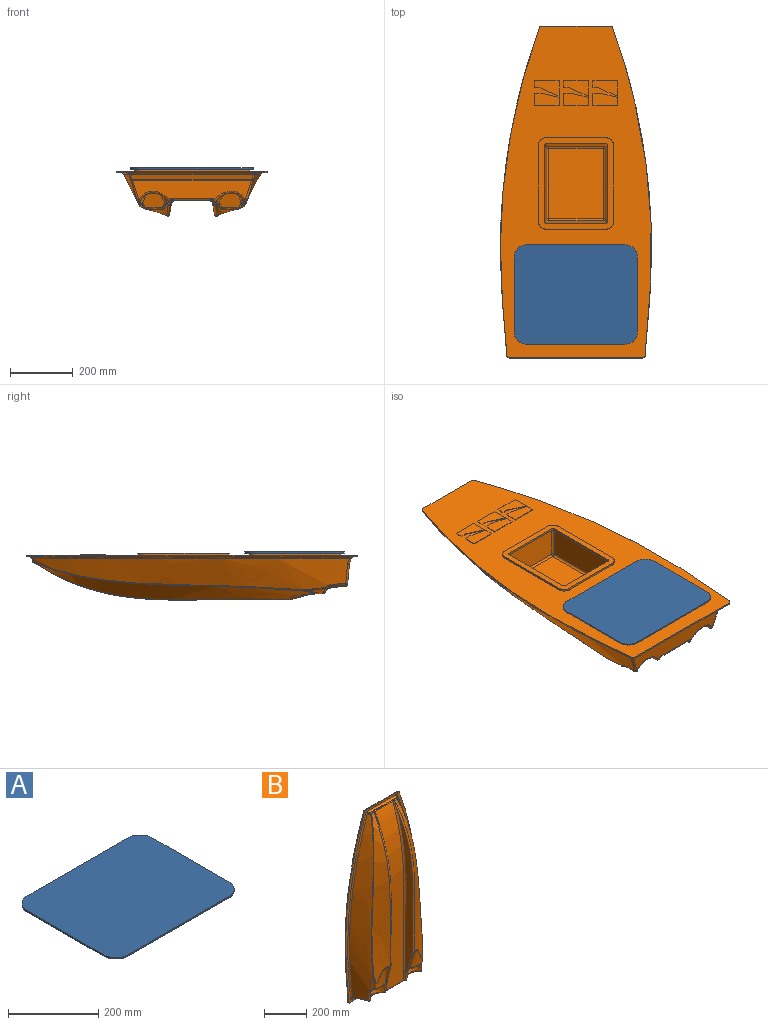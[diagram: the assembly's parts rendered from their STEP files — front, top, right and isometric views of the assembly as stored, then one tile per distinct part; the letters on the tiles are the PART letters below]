
ASSEMBLY  parts=2 mates=1
PART A: 10 faces, bbox 394x318x4 mm
  f0: plane 238x4mm, normal (-1,0,0), area 952mm2, adj f4,f5,f6,f9
  f1: plane 314x4mm, normal (0,-1,0), area 1256mm2, adj f4,f5,f6,f7
  f2: plane 238x4mm, normal (1,0,0), area 952mm2, adj f4,f5,f7,f8
  f3: plane 314x4mm, normal (0,1,0), area 1256mm2, adj f4,f5,f8,f9
  f4: plane 394x318mm, normal (0,0,1), area 123918.5mm2, adj f0,f1,f2,f3,f6,f7,f8,f9
  f5: plane 394x318mm, normal (0,0,-1), area 123918.5mm2, adj f0,f1,f2,f3,f6,f7,f8,f9
  f6: cylinder r=40mm len=40mm, axis (0,0,1), area 251.3mm2, adj f0,f1,f4,f5
  f7: cylinder r=40mm len=40mm, axis (0,0,-1), area 251.3mm2, adj f1,f2,f4,f5
  f8: cylinder r=40mm len=40mm, axis (0,0,1), area 251.3mm2, adj f2,f3,f4,f5
  f9: cylinder r=40mm len=40mm, axis (0,0,-1), area 251.3mm2, adj f0,f3,f4,f5
PART B: 255 faces, bbox 484.7x161.7x1062.5 mm
  f0: plane 1062.25x484.43mm, normal (0,1,0), area 254372.4mm2, adj f195,f196,f197,f198,f199,f200,f201,f202
  f1: sphere r=6.35mm, area 34mm2, adj f22,f26,f27
  f2: sphere r=6.35mm, area 34mm2, adj f32,f35,f36
  f3: sphere r=6.35mm, area 72.6mm2, adj f7,f8,f11,f40,f41
  f4: sphere r=6.35mm, area 72.6mm2, adj f10,f13,f14,f39,f42
  f5: sphere r=6.35mm, area 9.7mm2, adj f32,f43,f44
  f6: bspline ~1.26x0.54mm, area 0.2mm2, adj f31,f44,f45
  f7: bspline ~7.91x4.2mm, area 3.2mm2, adj f3,f11,f49,f87
  f8: bspline ~53.18x21.63mm, area 709.5mm2, adj f3,f22,f49,f69
  f9: bspline ~7.58x7.17mm, area 16mm2, adj f10,f39,f50
  f10: bspline ~9.73x6.62mm, area 49.8mm2, adj f4,f9,f14,f50
  f11: bspline ~9.73x6.62mm, area 49.8mm2, adj f3,f7,f12,f50
  f12: bspline ~7.58x7.17mm, area 16mm2, adj f11,f40,f50
  f13: bspline ~53.18x21.63mm, area 709.5mm2, adj f4,f35,f51,f80
  f14: bspline ~7.91x4.2mm, area 3.2mm2, adj f4,f10,f51,f87
  f15: bspline ~1016x132.22mm, area 25613.1mm2, adj f32,f35,f43,f53
  f16: sphere r=6.37mm, area 0.3mm2, adj f25,f56,f57
  f17: bspline ~1016x132.22mm, area 25875.6mm2, adj f22,f26,f47,f58
  f18: sphere r=6.35mm, area 9.7mm2, adj f26,f57,f58
  f19: bspline ~4.38x4.27mm, area 5.3mm2, adj f60,f62,f63
  f20: bspline ~4.38x4.27mm, area 5.3mm2, adj f61,f62,f65
  f21: plane 71.82x52.53mm, normal (0,-0.28,-0.96), area 2930.9mm2, adj f24,f28,f70
  f22: bspline ~16.78x12.12mm, area 106.9mm2, adj f1,f8,f17,f48,f70
  f23: bspline ~6.08x5.67mm, area 16.2mm2, adj f24,f28,f71
  f24: bspline ~14.85x9.65mm, area 114.2mm2, adj f21,f23,f29,f71
  f25: bspline ~1.31x0.96mm, area 0.2mm2, adj f16,f56,f71
  f26: bspline ~116.49x39.24mm, area 1463.5mm2, adj f1,f17,f18,f71
  f27: bspline ~9.52x6.58mm, area 40.3mm2, adj f1,f28,f70,f71
  f28: bspline ~70.09x19.29mm, area 611.2mm2, adj f21,f23,f27,f71
  f29: bspline ~6.82x6.46mm, area 30.8mm2, adj f24,f70,f71,f72
  f30: bspline ~14.85x9.65mm, area 114.2mm2, adj f34,f37,f38,f77
  f31: bspline ~1.31x0.96mm, area 0.2mm2, adj f6,f45,f77
  f32: bspline ~116.49x39.24mm, area 1463.5mm2, adj f2,f5,f15,f77
  f33: bspline ~70.09x19.29mm, area 611.5mm2, adj f34,f36,f37,f77
  f34: bspline ~6.08x5.68mm, area 16.4mm2, adj f30,f33,f77
  f35: bspline ~16.78x12.12mm, area 106.9mm2, adj f2,f13,f15,f52,f79
  f36: bspline ~9.52x6.58mm, area 40.3mm2, adj f2,f33,f77,f79
  f37: plane 71.84x52.56mm, normal (0,-0.28,-0.96), area 2942.6mm2, adj f30,f33,f79
  f38: bspline ~6.82x6.46mm, area 30.8mm2, adj f30,f77,f78,f79
  f39: cylinder r=6.35mm len=7.58mm, axis (0.19,-0.98,0.09), area 13.2mm2, adj f4,f9,f81
  f40: cylinder r=6.35mm len=7.58mm, axis (-0.19,-0.98,0.09), area 13.2mm2, adj f3,f12,f81
  f41: bspline ~99.88x34.31mm, area 1198.1mm2, adj f3,f68,f69,f81
  f42: bspline ~99.88x34.31mm, area 1198.1mm2, adj f4,f80,f81,f82
  f43: bspline ~808.3x116.97mm, area 9915.9mm2, adj f5,f15,f46,f54,f83
  f44: bspline ~78.04x73.35mm, area 166.7mm2, adj f5,f6,f77,f83
  f45: bspline ~36.3x12.19mm, area 128mm2, adj f6,f31,f76,f77,f83
  f46: bspline ~16.12x10.65mm, area 71.1mm2, adj f43,f83,f85,f86
  f47: bspline ~889.41x62.25mm, area 11708.5mm2, adj f17,f48,f55,f87
  f48: bspline ~9.35x7.68mm, area 24.4mm2, adj f22,f47,f49,f87
  f49: bspline ~53.05x9.28mm, area 561.9mm2, adj f7,f8,f48,f87
  f50: cylinder r=6.35mm len=137.44mm, axis (-1,0,0), area 1159.7mm2, adj f9,f10,f11,f12,f81,f87
  f51: bspline ~53.05x9.28mm, area 561.9mm2, adj f13,f14,f52,f87
  f52: bspline ~9.35x7.68mm, area 24.4mm2, adj f35,f51,f53,f87
  f53: bspline ~889.41x62.25mm, area 11708.5mm2, adj f15,f52,f54,f87
  f54: bspline ~40.35x22.55mm, area 450.1mm2, adj f43,f53,f86,f87
  f55: bspline ~40.35x22.55mm, area 450.1mm2, adj f47,f58,f87,f88
  f56: bspline ~36.24x12.18mm, area 128mm2, adj f16,f25,f71,f73,f89
  f57: bspline ~78.71x73.37mm, area 166.9mm2, adj f16,f18,f71,f89
  f58: bspline ~808.3x116.97mm, area 9915.9mm2, adj f17,f18,f55,f59,f89
  f59: bspline ~16.11x10.64mm, area 71.1mm2, adj f58,f88,f89,f90
  f60: cylinder r=6.35mm len=93.67mm, axis (0,0.28,0.96), area 661mm2, adj f19,f63,f92,f93,f94
  f61: bspline ~41.14x13.58mm, area 350.4mm2, adj f20,f65,f66,f97
  f62: cylinder r=6.35mm len=190.72mm, axis (1,0,0), area 330.4mm2, adj f19,f20,f92,f97
  f63: bspline ~41.14x13.58mm, area 350.4mm2, adj f19,f60,f64,f97
  f64: cylinder r=9.53mm len=55.64mm, axis (0.07,0,-1), area 692.6mm2, adj f63,f93,f95,f97
  f65: cylinder r=6.35mm len=93.67mm, axis (0,0.28,0.96), area 661mm2, adj f20,f61,f92,f98,f99
  f66: cylinder r=9.53mm len=55.64mm, axis (0.07,0,1), area 692.6mm2, adj f61,f97,f99,f100
  f67: plane 226.39x175.59mm, normal (0,1,0), area 39752mm2, adj f102,f104,f106,f108
  f68: sphere r=6.35mm, area 62.1mm2, adj f41,f110,f111
  f69: bspline ~106.87x59.93mm, area 5268.7mm2, adj f8,f41,f70,f111
  f70: bspline ~93.04x53.52mm, area 1854.7mm2, adj f21,f22,f27,f29,f69,f112
  f71: bspline ~135.93x101.85mm, area 7002.2mm2, adj f23,f24,f25,f26,f27,f28,f29,f56
  f72: sphere r=6.35mm, area 29.9mm2, adj f29,f112,f113
  f73: sphere r=6.35mm, area 2.8mm2, adj f56,f113,f114
  f74: bspline ~1.78x0.99mm, area 1.3mm2, adj f110,f115,f116,f152
  f75: bspline ~1.78x0.99mm, area 1.3mm2, adj f116,f117,f122,f152
  f76: sphere r=6.35mm, area 2.8mm2, adj f45,f118,f119
  f77: bspline ~135.93x101.85mm, area 7033.4mm2, adj f30,f31,f32,f33,f34,f36,f38,f44
  f78: sphere r=6.35mm, area 29.9mm2, adj f38,f119,f120
  f79: bspline ~93.04x53.52mm, area 1854.7mm2, adj f35,f36,f37,f38,f80,f120
  f80: bspline ~106.87x59.93mm, area 5268.7mm2, adj f13,f42,f79,f121
  f81: plane 380.28x66.84mm, normal (0,-0.09,-1), area 18542.7mm2, adj f39,f40,f41,f42,f50,f110,f116,f122
  f82: sphere r=6.35mm, area 62.1mm2, adj f42,f121,f122
  f83: bspline ~1001.39x135.86mm, area 56942mm2, adj f43,f44,f45,f46,f118,f124
  f84: sphere r=6.35mm, area 18.4mm2, adj f118,f123,f124
  f85: sphere r=6.35mm, area 5.8mm2, adj f46,f124,f125
  f86: bspline ~16.69x10.11mm, area 108.1mm2, adj f46,f54,f87,f125
  f87: extruded ~997.81x121.57mm, area 112470.9mm2, adj f7,f14,f47,f48,f49,f50,f51,f52
  f88: bspline ~16.67x10.1mm, area 108.1mm2, adj f55,f59,f87,f127
  f89: bspline ~1001.39x135.86mm, area 56952.2mm2, adj f56,f57,f58,f59,f114,f128
  f90: sphere r=6.35mm, area 5.8mm2, adj f59,f127,f128
  f91: sphere r=6.35mm, area 18.4mm2, adj f114,f128,f129
  f92: plane 307.85x195.35mm, normal (0,0.96,-0.28), area 43237.5mm2, adj f60,f62,f65,f130,f132,f134,f136,f137
  f93: plane 54.96x14.56mm, normal (-0.97,0.25,-0.07), area 414.3mm2, adj f60,f64,f138
  f94: sphere r=6.35mm, area 35.9mm2, adj f60,f137,f138
  f95: bspline ~9.25x7.16mm, area 37.6mm2, adj f64,f96,f97,f138
  f96: bspline ~11.71x11.12mm, area 43.8mm2, adj f95,f138,f139
  f97: plane 181.97x99.98mm, normal (0,1,0), area 16025.7mm2, adj f61,f62,f63,f64,f66,f95,f100,f139
  f98: sphere r=6.35mm, area 35.9mm2, adj f65,f136,f140
  f99: plane 54.96x14.56mm, normal (0.97,0.25,-0.07), area 414.3mm2, adj f65,f66,f140
  f100: bspline ~9.25x7.16mm, area 37.6mm2, adj f66,f97,f101,f140
  f101: bspline ~11.71x11.12mm, area 43.8mm2, adj f100,f139,f140
  f102: cylinder r=6.35mm len=175.59mm, axis (-1,0,0), area 1654.1mm2, adj f67,f103,f109,f142
  f103: sphere r=6.35mm, area 36.8mm2, adj f102,f104,f143
  f104: cylinder r=6.35mm len=226.39mm, axis (0,0,1), area 2132.7mm2, adj f67,f103,f105,f144
  f105: sphere r=6.35mm, area 36.8mm2, adj f104,f106,f145
  f106: cylinder r=6.35mm len=175.59mm, axis (1,0,0), area 1654.1mm2, adj f67,f105,f107,f146
  f107: sphere r=6.35mm, area 36.8mm2, adj f106,f108,f147
  f108: cylinder r=6.35mm len=226.39mm, axis (0,0,-1), area 2132.7mm2, adj f67,f107,f109,f148
  f109: sphere r=6.35mm, area 36.8mm2, adj f102,f108,f149
  f110: bspline ~66.29x26.55mm, area 633.7mm2, adj f68,f74,f81,f115,f150
  f111: bspline ~50.49x20.22mm, area 745mm2, adj f68,f69,f112,f150
  f112: bspline ~17.06x16.44mm, area 176.8mm2, adj f70,f72,f111,f150
  f113: bspline ~69.37x10.94mm, area 643.8mm2, adj f71,f72,f73,f150
  f114: bspline ~865.79x92.89mm, area 2954.9mm2, adj f73,f89,f91,f150
  f115: bspline ~6.08x6.08mm, area 6mm2, adj f74,f110,f151
  f116: cylinder r=6.99mm len=379.66mm, axis (-1,0,0), area 694.3mm2, adj f74,f75,f81,f152
  f117: bspline ~6.08x6.08mm, area 6mm2, adj f75,f122,f153
  f118: bspline ~865.79x92.89mm, area 2954.5mm2, adj f76,f83,f84,f154
  f119: bspline ~69.37x10.94mm, area 643.8mm2, adj f76,f77,f78,f154
  f120: bspline ~17.06x16.44mm, area 176.8mm2, adj f78,f79,f121,f154
  f121: bspline ~50.49x20.22mm, area 745mm2, adj f80,f82,f120,f154
  f122: bspline ~66.29x26.55mm, area 633.7mm2, adj f75,f81,f82,f117,f154
  f123: bspline ~8.16x7.77mm, area 42.6mm2, adj f84,f154,f156,f157
  f124: bspline ~18.89x7.34mm, area 113.9mm2, adj f83,f84,f85,f157
  f125: bspline ~6.94x6.26mm, area 37.5mm2, adj f85,f86,f126,f157
  f126: cylinder r=6.35mm len=121.57mm, axis (-1,0,0), area 825mm2, adj f87,f125,f127,f157
  f127: bspline ~6.94x6.26mm, area 37.5mm2, adj f88,f90,f126,f157
  f128: bspline ~18.89x7.34mm, area 113.9mm2, adj f89,f90,f91,f157
  f129: bspline ~8.16x7.77mm, area 42.6mm2, adj f91,f150,f157,f158
  f130: cylinder r=6.35mm len=197.1mm, axis (-0.02,-0.28,-0.96), area 1919.3mm2, adj f92,f131,f141,f160
  f131: sphere r=6.35mm, area 25.5mm2, adj f130,f132,f161
  f132: cylinder r=6.35mm len=307.85mm, axis (-1,0,0), area 2013mm2, adj f92,f131,f133,f162
  f133: sphere r=6.35mm, area 25.5mm2, adj f132,f134,f163
  f134: cylinder r=6.35mm len=197.1mm, axis (0.02,-0.28,-0.96), area 1919.3mm2, adj f92,f133,f135,f164
  f135: sphere r=6.35mm, area 39mm2, adj f134,f137,f165
  f136: cylinder r=6.35mm len=53.67mm, axis (-1,0,0), area 535.3mm2, adj f92,f98,f141,f166
  f137: cylinder r=6.35mm len=53.67mm, axis (-1,0,0), area 535.3mm2, adj f92,f94,f135,f166
  f138: cylinder r=6.35mm len=27.27mm, axis (-0.26,-0.93,0.27), area 206.8mm2, adj f93,f94,f95,f96,f166
  f139: cylinder r=6.35mm len=175.95mm, axis (1,0,0), area 1347mm2, adj f96,f97,f101,f166
  f140: cylinder r=6.35mm len=27.27mm, axis (-0.26,0.93,-0.27), area 206.8mm2, adj f98,f99,f100,f101,f166
  f141: sphere r=6.35mm, area 39mm2, adj f130,f136,f167
  f142: plane 190.55x85.48mm, normal (0,0.09,-1), area 15709.4mm2, adj f102,f143,f149,f168
  f143: cylinder r=6.35mm len=85.71mm, axis (-0.09,-0.99,-0.09), area 855mm2, adj f103,f142,f144,f169
  f144: plane 241.35x85.48mm, normal (-1,0.09,0), area 20068.6mm2, adj f104,f143,f145,f170
  f145: cylinder r=6.35mm len=85.71mm, axis (-0.09,-0.99,0.09), area 855mm2, adj f105,f144,f146,f171
  f146: plane 190.55x85.48mm, normal (0,0.09,1), area 15709.4mm2, adj f106,f145,f147,f172
  f147: cylinder r=6.35mm len=85.71mm, axis (0.09,-0.99,0.09), area 855mm2, adj f107,f146,f148,f173
  f148: plane 241.35x85.48mm, normal (1,0.09,0), area 20068.6mm2, adj f108,f147,f149,f174
  f149: cylinder r=6.35mm len=85.71mm, axis (0.09,-0.99,-0.09), area 855mm2, adj f109,f142,f148,f175
  f150: bspline ~1016x134.79mm, area 89372.7mm2, adj f110,f111,f112,f113,f114,f129,f151,f158
  f151: bspline ~18.27x11.89mm, area 160.3mm2, adj f115,f150,f152,f177
  f152: plane 390.83x15.99mm, normal (0,-0.34,-0.94), area 6510mm2, adj f74,f75,f116,f151,f153,f178
  f153: bspline ~18.27x11.89mm, area 160.3mm2, adj f117,f152,f154,f179
  f154: bspline ~1016x134.79mm, area 90363.1mm2, adj f118,f119,f120,f121,f122,f123,f153,f156
  f155: bspline ~10.8x8.5mm, area 23mm2, adj f156,f180,f181
  f156: bspline ~9.8x7.98mm, area 55.6mm2, adj f123,f154,f155,f181
  f157: plane 179.17x4.93mm, normal (0,-0.09,1), area 267.9mm2, adj f123,f124,f125,f126,f127,f128,f129,f181
  f158: bspline ~9.8x7.98mm, area 55.6mm2, adj f129,f150,f159,f181
  f159: bspline ~10.9x8.5mm, area 23.1mm2, adj f158,f176,f181
  f160: plane 241.13x109.59mm, normal (-1,0.09,0), area 18112.7mm2, adj f130,f161,f167,f182
  f161: cylinder r=6.35mm len=55.92mm, axis (0.08,0.96,0.26), area 554.3mm2, adj f131,f160,f162,f183,f184
  f162: plane 317.42x54.67mm, normal (0,0.26,-0.97), area 17694mm2, adj f132,f161,f163,f185
  f163: cylinder r=6.35mm len=55.84mm, axis (0.08,-0.96,-0.26), area 552.8mm2, adj f133,f162,f164,f186
  f164: plane 241.13x109.59mm, normal (1,0.09,0), area 18112.7mm2, adj f134,f163,f165,f187
  f165: cylinder r=6.35mm len=112.06mm, axis (0.08,-0.96,0.27), area 1129.9mm2, adj f135,f164,f166,f188
  f166: plane 317.44x110.79mm, normal (0,0.28,0.96), area 30416.8mm2, adj f136,f137,f138,f139,f140,f165,f167,f189
  f167: cylinder r=6.35mm len=112.13mm, axis (0.08,0.96,-0.27), area 1131.4mm2, adj f141,f160,f166,f190,f191
  f168: plane 190.55x6.35mm, normal (0,0,-1), area 1210mm2, adj f142,f169,f175,f192
  f169: extruded ~6.35x6.33mm, area 63.1mm2, adj f143,f168,f170,f192
  f170: plane 241.35x6.35mm, normal (-1,0,0), area 1532.6mm2, adj f144,f169,f171,f192
  f171: extruded ~6.35x6.33mm, area 63.1mm2, adj f145,f170,f172,f192
  f172: plane 190.55x6.35mm, normal (0,0,1), area 1210mm2, adj f146,f171,f173,f192
  f173: extruded ~6.35x6.33mm, area 63.1mm2, adj f147,f172,f174,f192
  f174: plane 241.35x6.35mm, normal (1,0,0), area 1532.6mm2, adj f148,f173,f175,f192
  f175: extruded ~6.35x6.33mm, area 63.1mm2, adj f149,f168,f174,f192
  f176: bspline ~1029.66x133.47mm, area 10632.5mm2, adj f150,f159,f177,f193
  f177: bspline ~14.9x14.64mm, area 168.3mm2, adj f151,f176,f178,f193
  f178: cylinder r=9.53mm len=390.82mm, axis (-1,0,0), area 4547.9mm2, adj f152,f177,f179,f193
  f179: bspline ~14.9x14.64mm, area 168.3mm2, adj f153,f178,f180,f193
  f180: bspline ~1029.66x133.47mm, area 10632.5mm2, adj f154,f155,f179,f193
  f181: cylinder r=9.53mm len=206.12mm, axis (1,0,0), area 2720.6mm2, adj f155,f156,f157,f158,f159,f193
  f182: plane 241.13x6.35mm, normal (-1,0,0), area 1531.2mm2, adj f160,f183,f191,f194
  f183: extruded ~6.35x6.12mm, area 50.9mm2, adj f161,f182,f184,f194
  f184: cylinder r=6.14mm len=6.35mm, axis (0,1,0), area 12.3mm2, adj f161,f183,f185,f194
  f185: plane 317.42x6.35mm, normal (0,0,-1), area 2015.6mm2, adj f162,f184,f186,f194
  f186: extruded ~6.43x6.35mm, area 63.2mm2, adj f163,f185,f187,f194
  f187: plane 241.13x6.35mm, normal (1,0,0), area 1531.2mm2, adj f164,f186,f188,f194
  f188: extruded ~6.45x6.35mm, area 63.3mm2, adj f165,f187,f189,f194
  f189: plane 317.44x6.35mm, normal (0,0,1), area 2015.7mm2, adj f166,f188,f190,f194
  f190: cylinder r=6.09mm len=6.35mm, axis (0,1,0), area 11.5mm2, adj f167,f189,f191,f194
  f191: extruded ~6.35x6.18mm, area 51.8mm2, adj f167,f182,f190,f194
  f192: plane 292.3x241.5mm, normal (0,1,0), area 18352.5mm2, adj f168,f169,f170,f171,f172,f173,f174,f175
  f193: plane 1062.49x484.68mm, normal (0,-1,0), area 36063.5mm2, adj f176,f177,f178,f179,f180,f181,f203,f204
  f194: plane 368.6x292.72mm, normal (0,1,0), area 23180.1mm2, adj f182,f183,f184,f185,f186,f187,f188,f189
  f195: plane 190.55x6.35mm, normal (0,0,1), area 1210mm2, adj f0,f192,f196,f202
  f196: extruded ~25.38x25.38mm, area 253.1mm2, adj f0,f192,f195,f197
  f197: plane 241.35x6.35mm, normal (-1,0,0), area 1532.6mm2, adj f0,f192,f196,f198
  f198: extruded ~25.38x25.38mm, area 253.1mm2, adj f0,f192,f197,f199
  f199: plane 190.55x6.35mm, normal (0,0,-1), area 1210mm2, adj f0,f192,f198,f200
  f200: extruded ~25.38x25.38mm, area 253.1mm2, adj f0,f192,f199,f201
  f201: plane 241.35x6.35mm, normal (1,0,0), area 1532.6mm2, adj f0,f192,f200,f202
  f202: extruded ~25.38x25.38mm, area 253.1mm2, adj f0,f192,f195,f201
  f203: plane 426.03x4.76mm, normal (0,0,-1), area 2029mm2, adj f0,f193,f204,f210
  f204: cylinder r=7.62mm len=7.59mm, axis (0,-1,0), area 53.6mm2, adj f0,f193,f203,f205
  f205: extruded ~1048.53x124.47mm, area 5066.8mm2, adj f0,f193,f204,f206
  f206: cylinder r=7.62mm len=7.16mm, axis (0,-1,0), area 44.3mm2, adj f0,f193,f205,f207
  f207: plane 219.21x4.76mm, normal (0,0,1), area 1044mm2, adj f0,f193,f206,f208
  f208: cylinder r=7.62mm len=7.16mm, axis (0,-1,0), area 44.3mm2, adj f0,f193,f207,f209
  f209: extruded ~1048.53x124.47mm, area 5066.5mm2, adj f0,f193,f208,f210
  f210: cylinder r=7.62mm len=7.59mm, axis (0,-1,0), area 53.6mm2, adj f0,f193,f203,f209
  f211: plane 241.13x6.35mm, normal (1,0,0), area 1531.2mm2, adj f0,f194,f212,f218
  f212: extruded ~25.48x25.28mm, area 253.2mm2, adj f0,f194,f211,f213
  f213: plane 317.42x6.35mm, normal (0,0,1), area 2015.6mm2, adj f0,f194,f212,f214
  f214: extruded ~25.48x25.28mm, area 253.2mm2, adj f0,f194,f213,f215
  f215: plane 241.13x6.35mm, normal (-1,0,0), area 1531.2mm2, adj f0,f194,f214,f216
  f216: extruded ~25.5x25.27mm, area 253.3mm2, adj f0,f194,f215,f217
  f217: plane 317.44x6.35mm, normal (0,0,-1), area 2015.7mm2, adj f0,f194,f216,f218
  f218: extruded ~25.5x25.27mm, area 253.3mm2, adj f0,f194,f211,f217
  f219: plane 57.33x13.91mm, normal (-0.24,0,0.97), area 93.7mm2, adj f0,f220,f223,f224
  f220: plane 21.02x1.59mm, normal (0,0,1), area 33.4mm2, adj f0,f219,f221,f224
  f221: plane 39.78x1.59mm, normal (1,0,0), area 63.2mm2, adj f0,f220,f222,f224
  f222: plane 78.35x1.59mm, normal (0,0,-1), area 124.4mm2, adj f0,f221,f223,f224
  f223: plane 25.87x1.59mm, normal (-1,0,0), area 41.1mm2, adj f0,f219,f222,f224
  f224: plane 78.35x39.78mm, normal (0,1,0), area 2718.1mm2, adj f219,f220,f221,f222,f223
  f225: plane 60.65x28.18mm, normal (0.42,0,-0.91), area 106.2mm2, adj f0,f226,f229,f230
  f226: plane 50.33x1.59mm, normal (-1,0,0), area 79.9mm2, adj f0,f225,f227,f230
  f227: plane 78.35x1.59mm, normal (0,0,1), area 124.4mm2, adj f0,f226,f228,f230
  f228: plane 22.14x1.59mm, normal (1,0,0), area 35.2mm2, adj f0,f227,f229,f230
  f229: plane 17.7x1.59mm, normal (0,0,-1), area 28.1mm2, adj f0,f225,f228,f230
  f230: plane 78.35x50.33mm, normal (0,1,0), area 2589.5mm2, adj f225,f226,f227,f228,f229
  f231: plane 78.35x1.59mm, normal (0,0,-1), area 124.4mm2, adj f0,f232,f235,f236
  f232: plane 25.87x1.59mm, normal (-1,0,0), area 41.1mm2, adj f0,f231,f233,f236
  f233: plane 57.33x13.91mm, normal (-0.24,0,0.97), area 93.7mm2, adj f0,f232,f234,f236
  f234: plane 21.02x1.59mm, normal (0,0,1), area 33.4mm2, adj f0,f233,f235,f236
  f235: plane 39.78x1.59mm, normal (1,0,0), area 63.2mm2, adj f0,f231,f234,f236
  f236: plane 78.35x39.78mm, normal (0,1,0), area 2718.1mm2, adj f231,f232,f233,f234,f235
  f237: plane 60.65x28.18mm, normal (0.42,0,-0.91), area 106.2mm2, adj f0,f238,f241,f242
  f238: plane 50.33x1.59mm, normal (-1,0,0), area 79.9mm2, adj f0,f237,f239,f242
  f239: plane 78.35x1.59mm, normal (0,0,1), area 124.4mm2, adj f0,f238,f240,f242
  f240: plane 22.14x1.59mm, normal (1,0,0), area 35.2mm2, adj f0,f239,f241,f242
  f241: plane 17.7x1.59mm, normal (0,0,-1), area 28.1mm2, adj f0,f237,f240,f242
  f242: plane 78.35x50.33mm, normal (0,1,0), area 2589.5mm2, adj f237,f238,f239,f240,f241
  f243: plane 78.35x1.59mm, normal (0,0,-1), area 124.4mm2, adj f0,f244,f247,f248
  f244: plane 25.87x1.59mm, normal (-1,0,0), area 41.1mm2, adj f0,f243,f245,f248
  f245: plane 57.33x13.91mm, normal (-0.24,0,0.97), area 93.7mm2, adj f0,f244,f246,f248
  f246: plane 21.02x1.59mm, normal (0,0,1), area 33.4mm2, adj f0,f245,f247,f248
  f247: plane 39.78x1.59mm, normal (1,0,0), area 63.2mm2, adj f0,f243,f246,f248
  f248: plane 78.35x39.78mm, normal (0,1,0), area 2718.1mm2, adj f243,f244,f245,f246,f247
  f249: plane 60.65x28.18mm, normal (0.42,0,-0.91), area 106.2mm2, adj f0,f250,f253,f254
  f250: plane 50.33x1.59mm, normal (-1,0,0), area 79.9mm2, adj f0,f249,f251,f254
  f251: plane 78.35x1.59mm, normal (0,0,1), area 124.4mm2, adj f0,f250,f252,f254
  f252: plane 22.14x1.59mm, normal (1,0,0), area 35.2mm2, adj f0,f251,f253,f254
  f253: plane 17.7x1.59mm, normal (0,0,-1), area 28.1mm2, adj f0,f249,f252,f254
  f254: plane 78.35x50.33mm, normal (0,1,0), area 2589.5mm2, adj f249,f250,f251,f252,f253
PLACE A rot(axis=(1,0,0),180deg) t=(-263.26,-905.18,-200.06)mm
PLACE B rot(axis=(0,0.71,0.71),180deg) t=(-65.76,-206.54,-210.41)mm
MATE planar A.f4 <-> B.f194  axis (0,0,-1) through (-66.26,-1064.18,-204.06)mm
